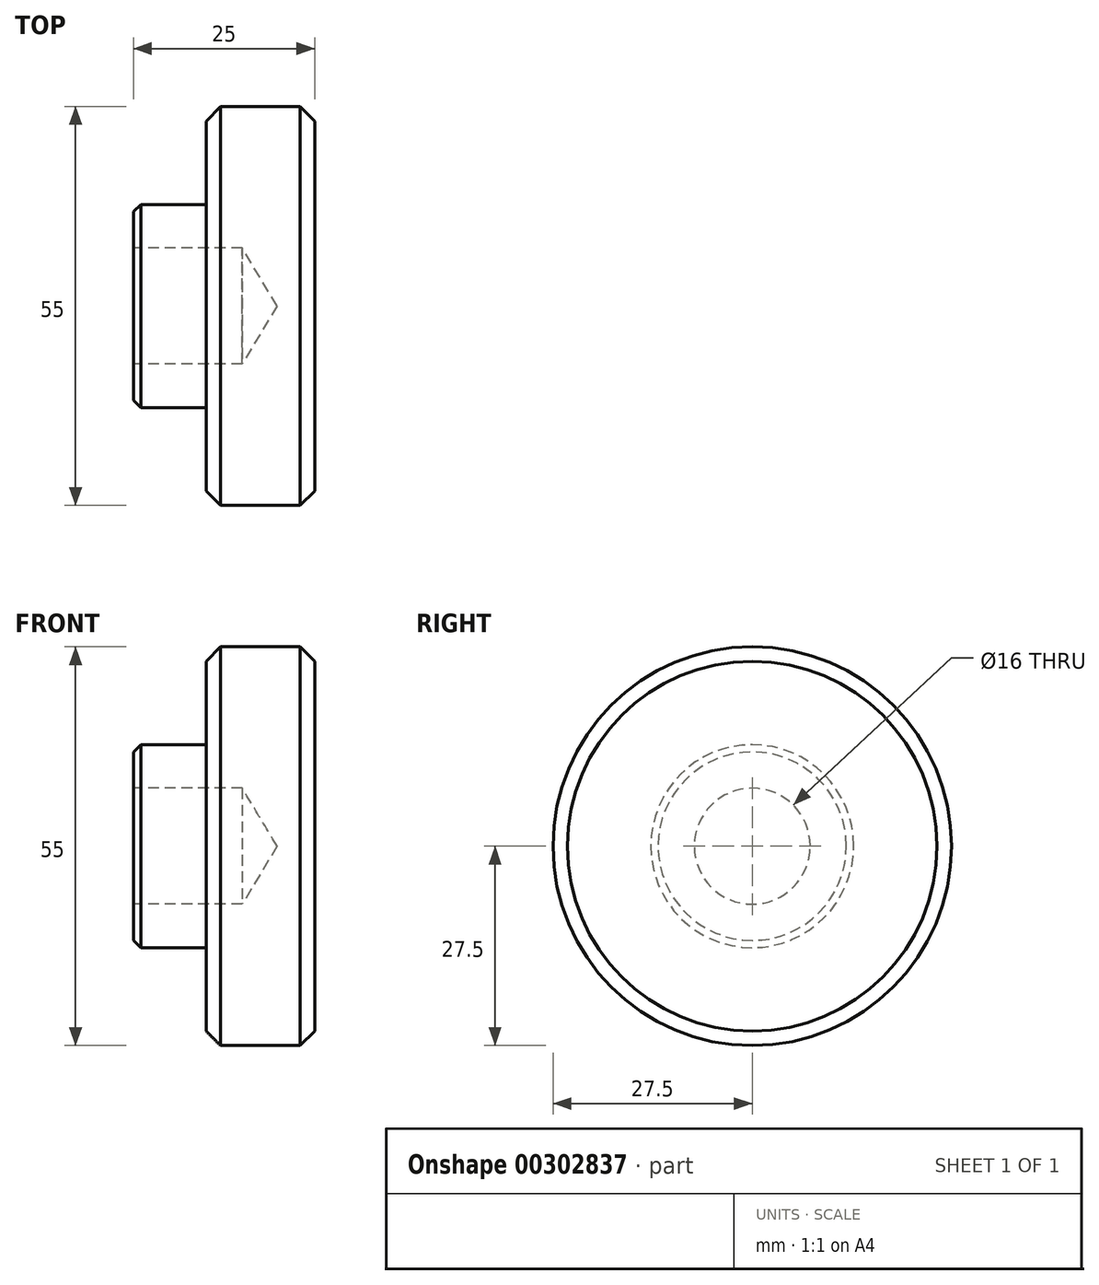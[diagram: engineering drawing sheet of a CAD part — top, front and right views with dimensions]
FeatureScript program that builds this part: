
annotation { "Feature Type Name" : "Feature", "Feature Type Description" : "" }
export const myFeature = defineFeature(function(context is Context, id is Id, definition is map)
    precondition{}
    {
        {
            var Q0;
            Q0=qCreatedBy(makeId("Front.planeOp"),FACE);
            var sketch = newSketch(context, id + "F0", { "sketchPlane" : qUnion([Q0])});
            skLineSegment(sketch, "E0", {"start": v(0, 0) * mm, "end": v(0, 14) * mm});
            skLineSegment(sketch, "E1", {"start": v(0, 14) * mm, "end": v(10, 14) * mm});
            skLineSegment(sketch, "E2", {"start": v(10, 14) * mm, "end": v(10, 27.5) * mm});
            skLineSegment(sketch, "E3", {"start": v(10, 27.5) * mm, "end": v(25, 27.5) * mm});
            skLineSegment(sketch, "E4", {"start": v(25, 27.5) * mm, "end": v(25, 0) * mm});
            skLineSegment(sketch, "E5", {"start": v(25, 0) * mm, "end": v(0, 0) * mm});
            skSolve(sketch);
        }
        {
            var Q0;
            Q0=makeQuery(id+"F0.imprint","IMPRINT",FACE,{"disambiguationData":[TD([[makeQuery(id+"F0.imprint","IMPRINT",EDGE,{"derivedFrom":sQuery(id+"F0.wireOp",EDGE,"E0")}),-1.0]])]});
            var Q1;
            Q1=sQuery(id+"F0.wireOp",EDGE,"E5");
            revolve(context, id + "F1", {"entities" : qUnion([Q0]), "axis" : qUnion([Q1]), "revolveType" : RevolveType.FULL});
        }
        {
            var Q0;
            Q0=makeQuery(id+"F1.opRevolve","SWEPT_FACE",FACE,{"disambiguationData":[OSD([sQuery(id+"F0.wireOp",EDGE,"E0")])]});
            var sketch = newSketch(context, id + "F2", { "sketchPlane" : qUnion([Q0])});
            skPoint(sketch, "E6", {"position": v(0, 0) * mm});
            skSolve(sketch);
        }
        {
            var Q0;
            Q0=sQuery(id+"F2.wireOp",VERTEX,"E6");
            var Q1;
            Q1=makeQuery(id+"F1.opRevolve","SWEPT_BODY",BODY,{"disambiguationData":[OSD([sQuery(id+"F0.wireOp",EDGE,"E0"),sQuery(id+"F0.wireOp",EDGE,"E1"),sQuery(id+"F0.wireOp",EDGE,"E2"),sQuery(id+"F0.wireOp",EDGE,"E3"),sQuery(id+"F0.wireOp",EDGE,"E4"),sQuery(id+"F0.wireOp",EDGE,"E5")])]});
            hole(context, id + "F3", {"style" : HoleStyle.SIMPLE, "endStyle" : HoleEndStyle.BLIND, "holeDiameter" : 16 * mm, "holeDepth" : 15 * mm, "tappedDepth" : 12 * mm, "tapClearance" : 3, "startFromSketch" : true, "locations" : qUnion([Q0]), "scope" : qUnion([Q1])});
        }
        {
            var Q0;
            Q0=makeQuery(id+"F1.opRevolve","SWEPT_FACE",FACE,{"disambiguationData":[OSD([sQuery(id+"F0.wireOp",EDGE,"E3")])]});
            chamfer(context, id + "F4", {"entities" : qUnion([Q0]), "width" : 2 * mm, "tangentPropagation" : true});
        }
        {
            var Q0;
            Q0=makeQuery(id+"F1.opRevolve","SWEPT_EDGE",EDGE,{"disambiguationData":[OSD([sQuery(id+"F0.wireOp",EDGE,"E0"),sQuery(id+"F0.wireOp",EDGE,"E1")])]});
            chamfer(context, id + "F5", {"entities" : qUnion([Q0]), "width" : 1 * mm, "tangentPropagation" : true});
        }
    });
